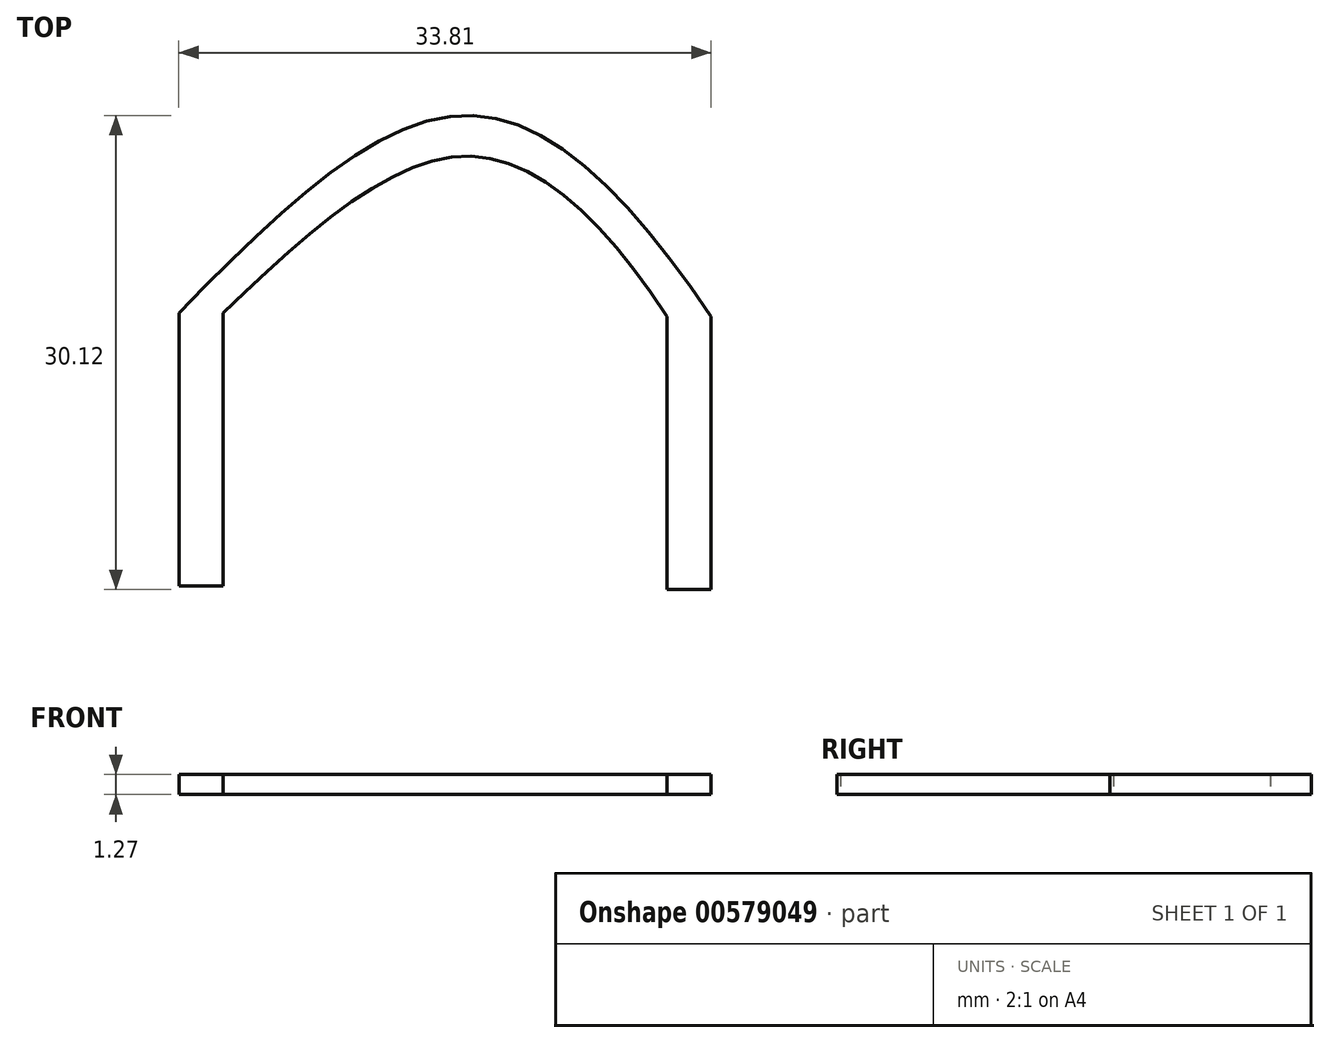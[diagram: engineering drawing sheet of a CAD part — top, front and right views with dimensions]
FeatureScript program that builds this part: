
annotation { "Feature Type Name" : "Feature", "Feature Type Description" : "" }
export const myFeature = defineFeature(function(context is Context, id is Id, definition is map)
    precondition{}
    {
        {
            var Q0;
            Q0=qCreatedBy(makeId("Top.planeOp"),FACE);
            var sketch = newSketch(context, id + "F0", { "sketchPlane" : qUnion([Q0])});
            skLineSegment(sketch, "E0.bottom", {"start": v(-18.4, 2.56) * mm, "end": v(-15.59, 2.56) * mm});
            skLineSegment(sketch, "E0.top", {"start": v(-18.4, 19.9) * mm, "end": v(-15.59, 19.9) * mm});
            skLineSegment(sketch, "E0.left", {"start": v(-18.4, 2.56) * mm, "end": v(-18.4, 19.9) * mm});
            skLineSegment(sketch, "E0.right", {"start": v(-15.59, 2.56) * mm, "end": v(-15.59, 19.9) * mm});
            skFitSpline(sketch, "E1", {"points": [v(-18.4, 19.9) * mm, v(0, 32.46) * mm, v(15.4, 19.68) * mm], "startDerivative": vector(37.99, 39.07) * mm, "endDerivative": vector(30.04, -44.82) * mm});
            skFitSpline(sketch, "E2", {"points": [v(-15.59, 19.9) * mm, v(0, 29.86) * mm, v(12.58, 19.68) * mm], "startDerivative": vector(32.34, 31.26) * mm, "endDerivative": vector(23.98, -37.07) * mm});
            skLineSegment(sketch, "E3", {"start": v(12.58, 19.68) * mm, "end": v(15.4, 19.68) * mm});
            skLineSegment(sketch, "E4.top", {"start": v(12.58, 2.34) * mm, "end": v(15.4, 2.34) * mm});
            skLineSegment(sketch, "E4.left", {"start": v(12.58, 19.68) * mm, "end": v(12.58, 2.34) * mm});
            skLineSegment(sketch, "E4.right", {"start": v(15.4, 19.68) * mm, "end": v(15.4, 2.34) * mm});
            skSolve(sketch);
        }
        {
            var Q0;
            Q0=makeQuery(id+"F0.imprint","IMPRINT",FACE,{"disambiguationData":[TD([[makeQuery(id+"F0.imprint","IMPRINT",EDGE,{"derivedFrom":sQuery(id+"F0.wireOp",EDGE,"E0.top")}),1.0]])]});
            var Q1;
            Q1=makeQuery(id+"F0.imprint","IMPRINT",FACE,{"disambiguationData":[TD([[makeQuery(id+"F0.imprint","IMPRINT",EDGE,{"derivedFrom":sQuery(id+"F0.wireOp",EDGE,"E0.bottom")}),1.0]])]});
            var Q2;
            Q2=makeQuery(id+"F0.imprint","IMPRINT",FACE,{"disambiguationData":[TD([[makeQuery(id+"F0.imprint","IMPRINT",EDGE,{"derivedFrom":sQuery(id+"F0.wireOp",EDGE,"E3")}),-1.0]])]});
            extrude(context, id + "F1", {"entities" : qUnion([Q0, Q1, Q2]), "depth" : 1.27 * mm, "offsetDistance" : 25.4 * mm});
        }
    });
